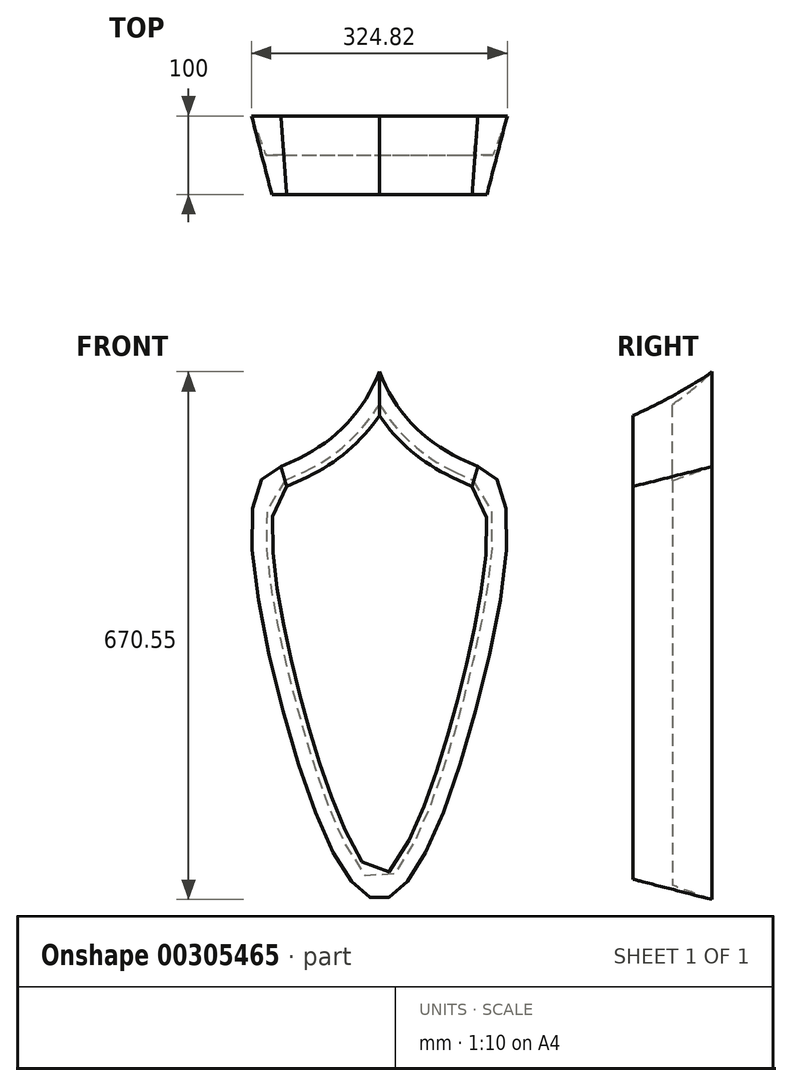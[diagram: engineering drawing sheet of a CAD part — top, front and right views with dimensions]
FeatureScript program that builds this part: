
annotation { "Feature Type Name" : "Feature", "Feature Type Description" : "" }
export const myFeature = defineFeature(function(context is Context, id is Id, definition is map)
    precondition{}
    {
        {
            var Q0;
            Q0=qCreatedBy(makeId("Front.planeOp"),FACE);
            var sketch = newSketch(context, id + "F0", { "sketchPlane" : qUnion([Q0])});
            skLineSegment(sketch, "E0.bottom", {"start": v(125, -150) * mm, "end": v(-125, -150) * mm, "construction": true});
            skLineSegment(sketch, "E0.top", {"start": v(125, 150) * mm, "end": v(-125, 150) * mm});
            skLineSegment(sketch, "E0.left", {"start": v(125, -150) * mm, "end": v(125, 150) * mm, "construction": true});
            skLineSegment(sketch, "E0.right", {"start": v(-125, -150) * mm, "end": v(-125, 150) * mm, "construction": true});
            skPoint(sketch, "E0.middle", {"position": v(0, 0) * mm});
            skCircle(sketch, "E1", {"center": v(-186.87, 341.83) * mm, "radius": 200 * mm});
            skLineSegment(sketch, "E2", {"start": v(-125, 150) * mm, "end": v(-102.34, 160.57) * mm});
            skLineSegment(sketch, "E3", {"start": v(0, 0) * mm, "end": v(0, 350) * mm, "construction": true});
            skCircle(sketch, "E4.MirrorC", {"center": v(186.87, 341.83) * mm, "radius": 200 * mm});
            skLineSegment(sketch, "E5.MirrorCS", {"start": v(-125, 150) * mm, "end": v(125, 150) * mm, "construction": true});
            skLineSegment(sketch, "E6.MirrorCS", {"start": v(125, 150) * mm, "end": v(102.34, 160.57) * mm});
            skLineSegment(sketch, "E7", {"start": v(0, 0) * mm, "end": v(0, -400) * mm, "construction": true});
            skFitSpline(sketch, "E8", {"points": [v(-125, 150) * mm, v(-125, -150) * mm, v(0, -400) * mm, v(125, -150) * mm, v(125, 150) * mm], "startDerivative": vector(-729.5, -96.37) * mm, "endDerivative": vector(-729.5, 96.37) * mm});
            skSolve(sketch);
        }
        {
            var Q0;
            Q0=makeQuery(id+"F0.imprint","IMPRINT",FACE,{"disambiguationData":[TD([[makeQuery(id+"F0.imprint","IMPRINT",EDGE,{"derivedFrom":sQuery(id+"F0.wireOp",EDGE,"E0.top")}),1.0]])]});
            var Q1;
            Q1=makeQuery(id+"F0.imprint","IMPRINT",FACE,{"disambiguationData":[TD([[makeQuery(id+"F0.imprint","IMPRINT",EDGE,{"derivedFrom":sQuery(id+"F0.wireOp",EDGE,"E0.top")}),-1.0]])]});
            extrude(context, id + "F1", {"entities" : qUnion([Q0, Q1]), "depth" : 100 * mm, "hasDraft" : true, "draftAngle" : 14.5 * degree, "draftPullDirection" : true});
        }
        {
            var Q0;
            Q0=makeQuery(id+"F1.opExtrude","CAP_FACE",FACE,{"disambiguationData":[OSD([sQuery(id+"F0.wireOp",EDGE,"E1"),sQuery(id+"F0.wireOp",EDGE,"E2"),sQuery(id+"F0.wireOp",EDGE,"E4.MirrorC"),sQuery(id+"F0.wireOp",EDGE,"E6.MirrorCS"),sQuery(id+"F0.wireOp",EDGE,"E8")])],"isStart":true});
            extrude(context, id + "F2", {"entities" : qUnion([Q0]), "operationType" : NewBodyOperationType.REMOVE, "oppositeDirection" : true, "depth" : 50 * mm, "hasDraft" : true, "draftAngle" : 20 * degree, "draftPullDirection" : true});
        }
    });
